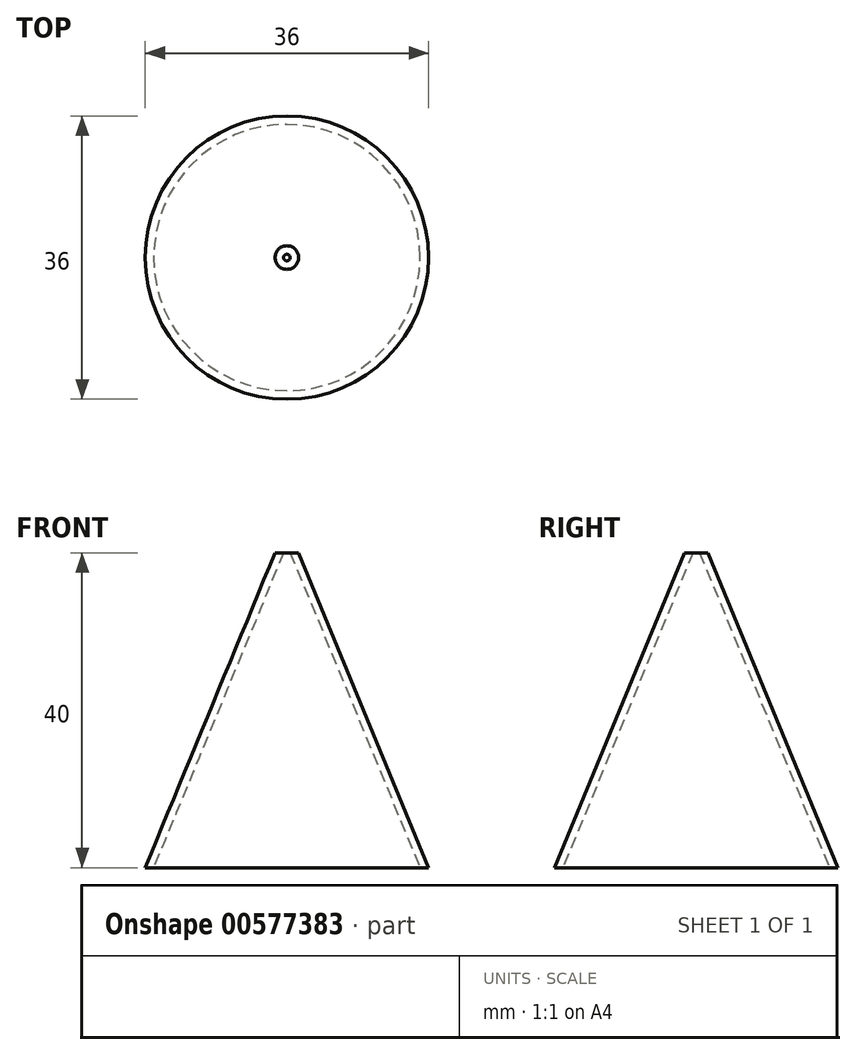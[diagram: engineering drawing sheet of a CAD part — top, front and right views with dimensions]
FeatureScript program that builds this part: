
annotation { "Feature Type Name" : "Feature", "Feature Type Description" : "" }
export const myFeature = defineFeature(function(context is Context, id is Id, definition is map)
    precondition{}
    {
        {
            var Q0;
            Q0=qCreatedBy(makeId("Front.planeOp"),FACE);
            var sketch = newSketch(context, id + "F0", { "sketchPlane" : qUnion([Q0])});
            skLineSegment(sketch, "E0.bottom", {"start": v(0, 0) * mm, "end": v(1.5, 0) * mm});
            skLineSegment(sketch, "E0.top", {"start": v(0, 40) * mm, "end": v(1.5, 40) * mm});
            skLineSegment(sketch, "E0.left", {"start": v(0, 0) * mm, "end": v(0, 40) * mm});
            skLineSegment(sketch, "E0.right", {"start": v(1.5, 0) * mm, "end": v(1.5, 40) * mm});
            skLineSegment(sketch, "E1.bottom", {"start": v(0, 0) * mm, "end": v(18, 0) * mm});
            skLineSegment(sketch, "E1.top", {"start": v(0, 9.86) * mm, "end": v(18, 9.86) * mm});
            skLineSegment(sketch, "E1.left", {"start": v(0, 0) * mm, "end": v(0, 9.86) * mm});
            skLineSegment(sketch, "E1.right", {"start": v(18, 0) * mm, "end": v(18, 9.86) * mm});
            skLineSegment(sketch, "E2", {"start": v(1.5, 40) * mm, "end": v(18, 0) * mm});
            skLineSegment(sketch, "E3", {"start": v(0.42, 40) * mm, "end": v(16.92, 0) * mm});
            skSolve(sketch);
        }
        {
            var Q0;
            {var subQ0=sQuery(id+"F0.wireOp",EDGE,"E2");var subQ5=sQuery(id+"F0.wireOp",EDGE,"E1.top");var subQ6=makeQuery(id+"F0.imprint","INTERSECT",VERTEX,{"derivedFrom":[subQ5,subQ0]});Q0=makeQuery(id+"F0.imprint","IMPRINT",FACE,{"disambiguationData":[TD([[makeQuery(id+"F0.imprint","IMPRINT",EDGE,{"disambiguationData":[TD([[subQ6,1.0]])],"derivedFrom":subQ5}),-1.0]])]});}
            var Q1;
            {var subQ0=sQuery(id+"F0.wireOp",EDGE,"E2");var subQ5=sQuery(id+"F0.wireOp",EDGE,"E1.top");var subQ6=makeQuery(id+"F0.imprint","INTERSECT",VERTEX,{"derivedFrom":[subQ5,subQ0]});Q1=makeQuery(id+"F0.imprint","IMPRINT",FACE,{"disambiguationData":[TD([[makeQuery(id+"F0.imprint","IMPRINT",EDGE,{"disambiguationData":[TD([[subQ6,1.0]])],"derivedFrom":subQ5}),1.0]])]});}
            var Q2;
            {var subQ1=sQuery(id+"F0.wireOp",EDGE,"E0.top");var subQ3=sQuery(id+"F0.wireOp",EDGE,"E3");var subQ4=makeQuery(id+"F0.imprint","INTERSECT",VERTEX,{"derivedFrom":[subQ1,subQ3]});Q2=makeQuery(id+"F0.imprint","IMPRINT",FACE,{"disambiguationData":[TD([[makeQuery(id+"F0.imprint","IMPRINT",EDGE,{"disambiguationData":[TD([[subQ4,-1.0]])],"derivedFrom":subQ3}),1.0]])]});}
            var Q3;
            Q3=sQuery(id+"F0.wireOp",EDGE,"E0.left");
            revolve(context, id + "F1", {"entities" : qUnion([Q0, Q1, Q2]), "axis" : qUnion([Q3]), "revolveType" : RevolveType.FULL});
        }
    });
